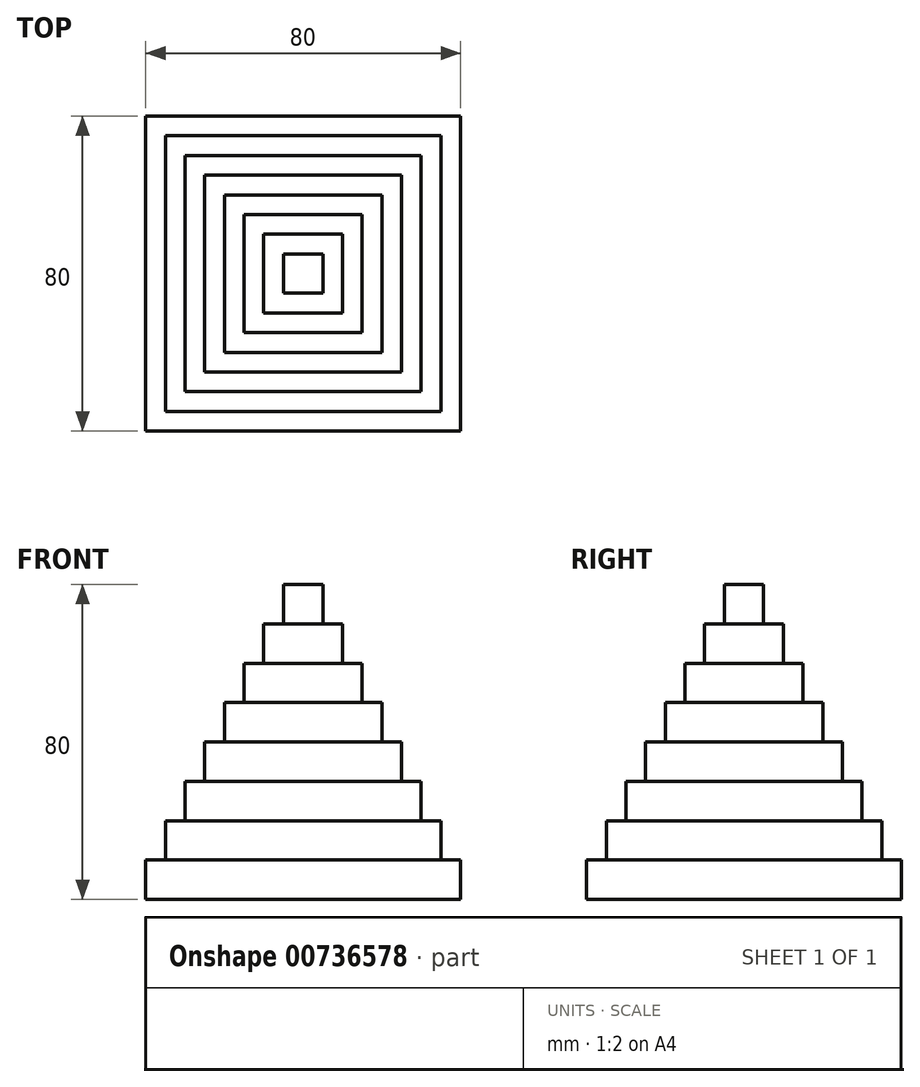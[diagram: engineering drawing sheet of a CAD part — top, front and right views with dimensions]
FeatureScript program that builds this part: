
annotation { "Feature Type Name" : "Feature", "Feature Type Description" : "" }
export const myFeature = defineFeature(function(context is Context, id is Id, definition is map)
    precondition{}
    {
        {
            var Q0;
            Q0=qCreatedBy(makeId("Top.planeOp"),FACE);
            var sketch = newSketch(context, id + "F0", { "sketchPlane" : qUnion([Q0])});
            skLineSegment(sketch, "E0.bottom", {"start": v(40, -40) * mm, "end": v(-40, -40) * mm});
            skLineSegment(sketch, "E0.top", {"start": v(40, 40) * mm, "end": v(-40, 40) * mm});
            skLineSegment(sketch, "E0.left", {"start": v(40, -40) * mm, "end": v(40, 40) * mm});
            skLineSegment(sketch, "E0.right", {"start": v(-40, -40) * mm, "end": v(-40, 40) * mm});
            skPoint(sketch, "E0.middle", {"position": v(0, 0) * mm});
            skLineSegment(sketch, "E1.bottom", {"start": v(35, -35) * mm, "end": v(-35, -35) * mm});
            skLineSegment(sketch, "E1.top", {"start": v(35, 35) * mm, "end": v(-35, 35) * mm});
            skLineSegment(sketch, "E1.left", {"start": v(35, -35) * mm, "end": v(35, 35) * mm});
            skLineSegment(sketch, "E1.right", {"start": v(-35, -35) * mm, "end": v(-35, 35) * mm});
            skLineSegment(sketch, "E2.bottom", {"start": v(30, -30) * mm, "end": v(-30, -30) * mm});
            skLineSegment(sketch, "E2.top", {"start": v(30, 30) * mm, "end": v(-30, 30) * mm});
            skLineSegment(sketch, "E2.left", {"start": v(30, -30) * mm, "end": v(30, 30) * mm});
            skLineSegment(sketch, "E2.right", {"start": v(-30, -30) * mm, "end": v(-30, 30) * mm});
            skLineSegment(sketch, "E3.bottom", {"start": v(25, -25) * mm, "end": v(-25, -25) * mm});
            skLineSegment(sketch, "E3.top", {"start": v(25, 25) * mm, "end": v(-25, 25) * mm});
            skLineSegment(sketch, "E3.left", {"start": v(25, -25) * mm, "end": v(25, 25) * mm});
            skLineSegment(sketch, "E3.right", {"start": v(-25, -25) * mm, "end": v(-25, 25) * mm});
            skLineSegment(sketch, "E4.bottom", {"start": v(20, -20) * mm, "end": v(-20, -20) * mm});
            skLineSegment(sketch, "E4.top", {"start": v(20, 20) * mm, "end": v(-20, 20) * mm});
            skLineSegment(sketch, "E4.left", {"start": v(20, -20) * mm, "end": v(20, 20) * mm});
            skLineSegment(sketch, "E4.right", {"start": v(-20, -20) * mm, "end": v(-20, 20) * mm});
            skLineSegment(sketch, "E5.bottom", {"start": v(15, -15) * mm, "end": v(-15, -15) * mm});
            skLineSegment(sketch, "E5.top", {"start": v(15, 15) * mm, "end": v(-15, 15) * mm});
            skLineSegment(sketch, "E5.left", {"start": v(15, -15) * mm, "end": v(15, 15) * mm});
            skLineSegment(sketch, "E5.right", {"start": v(-15, -15) * mm, "end": v(-15, 15) * mm});
            skLineSegment(sketch, "E6.bottom", {"start": v(10, -10) * mm, "end": v(-10, -10) * mm});
            skLineSegment(sketch, "E6.top", {"start": v(10, 10) * mm, "end": v(-10, 10) * mm});
            skLineSegment(sketch, "E6.left", {"start": v(10, -10) * mm, "end": v(10, 10) * mm});
            skLineSegment(sketch, "E6.right", {"start": v(-10, -10) * mm, "end": v(-10, 10) * mm});
            skLineSegment(sketch, "E7.bottom", {"start": v(5, -5) * mm, "end": v(-5, -5) * mm});
            skLineSegment(sketch, "E7.top", {"start": v(5, 5) * mm, "end": v(-5, 5) * mm});
            skLineSegment(sketch, "E7.left", {"start": v(5, -5) * mm, "end": v(5, 5) * mm});
            skLineSegment(sketch, "E7.right", {"start": v(-5, -5) * mm, "end": v(-5, 5) * mm});
            skSolve(sketch);
        }
        {
            var Q0;
            Q0=makeQuery(id+"F0.imprint","IMPRINT",FACE,{"disambiguationData":[TD([[makeQuery(id+"F0.imprint","IMPRINT",EDGE,{"derivedFrom":sQuery(id+"F0.wireOp",EDGE,"E0.bottom")}),-1.0]])]});
            extrude(context, id + "F1", {"entities" : qUnion([Q0]), "depth" : 10 * mm, "offsetDistance" : 25 * mm});
        }
        {
            var Q0;
            Q0=makeQuery(id+"F0.imprint","IMPRINT",FACE,{"disambiguationData":[TD([[makeQuery(id+"F0.imprint","IMPRINT",EDGE,{"derivedFrom":sQuery(id+"F0.wireOp",EDGE,"E1.bottom")}),-1.0]])]});
            extrude(context, id + "F2", {"entities" : qUnion([Q0]), "operationType" : NewBodyOperationType.ADD, "depth" : 20 * mm, "offsetDistance" : 25 * mm});
        }
        {
            var Q0;
            Q0=makeQuery(id+"F0.imprint","IMPRINT",FACE,{"disambiguationData":[TD([[makeQuery(id+"F0.imprint","IMPRINT",EDGE,{"derivedFrom":sQuery(id+"F0.wireOp",EDGE,"E2.bottom")}),-1.0]])]});
            extrude(context, id + "F3", {"entities" : qUnion([Q0]), "operationType" : NewBodyOperationType.ADD, "depth" : 30 * mm, "offsetDistance" : 25 * mm});
        }
        {
            var Q0;
            Q0=makeQuery(id+"F0.imprint","IMPRINT",FACE,{"disambiguationData":[TD([[makeQuery(id+"F0.imprint","IMPRINT",EDGE,{"derivedFrom":sQuery(id+"F0.wireOp",EDGE,"E3.bottom")}),-1.0]])]});
            extrude(context, id + "F4", {"entities" : qUnion([Q0]), "operationType" : NewBodyOperationType.ADD, "depth" : 40 * mm, "offsetDistance" : 25 * mm});
        }
        {
            var Q0;
            Q0=makeQuery(id+"F0.imprint","IMPRINT",FACE,{"disambiguationData":[TD([[makeQuery(id+"F0.imprint","IMPRINT",EDGE,{"derivedFrom":sQuery(id+"F0.wireOp",EDGE,"E4.bottom")}),-1.0]])]});
            extrude(context, id + "F5", {"entities" : qUnion([Q0]), "operationType" : NewBodyOperationType.ADD, "depth" : 50 * mm, "offsetDistance" : 25 * mm});
        }
        {
            var Q0;
            Q0=makeQuery(id+"F0.imprint","IMPRINT",FACE,{"disambiguationData":[TD([[makeQuery(id+"F0.imprint","IMPRINT",EDGE,{"derivedFrom":sQuery(id+"F0.wireOp",EDGE,"E5.bottom")}),-1.0]])]});
            extrude(context, id + "F6", {"entities" : qUnion([Q0]), "operationType" : NewBodyOperationType.ADD, "depth" : 60 * mm, "offsetDistance" : 25 * mm});
        }
        {
            var Q0;
            Q0=makeQuery(id+"F0.imprint","IMPRINT",FACE,{"disambiguationData":[TD([[makeQuery(id+"F0.imprint","IMPRINT",EDGE,{"derivedFrom":sQuery(id+"F0.wireOp",EDGE,"E6.bottom")}),-1.0]])]});
            extrude(context, id + "F7", {"entities" : qUnion([Q0]), "operationType" : NewBodyOperationType.ADD, "depth" : 70 * mm, "offsetDistance" : 25 * mm});
        }
        {
            var Q0;
            Q0=makeQuery(id+"F0.imprint","IMPRINT",FACE,{"disambiguationData":[TD([[makeQuery(id+"F0.imprint","IMPRINT",EDGE,{"derivedFrom":sQuery(id+"F0.wireOp",EDGE,"E7.bottom")}),-1.0]])]});
            extrude(context, id + "F8", {"entities" : qUnion([Q0]), "operationType" : NewBodyOperationType.ADD, "depth" : 80 * mm, "offsetDistance" : 25 * mm});
        }
    });
